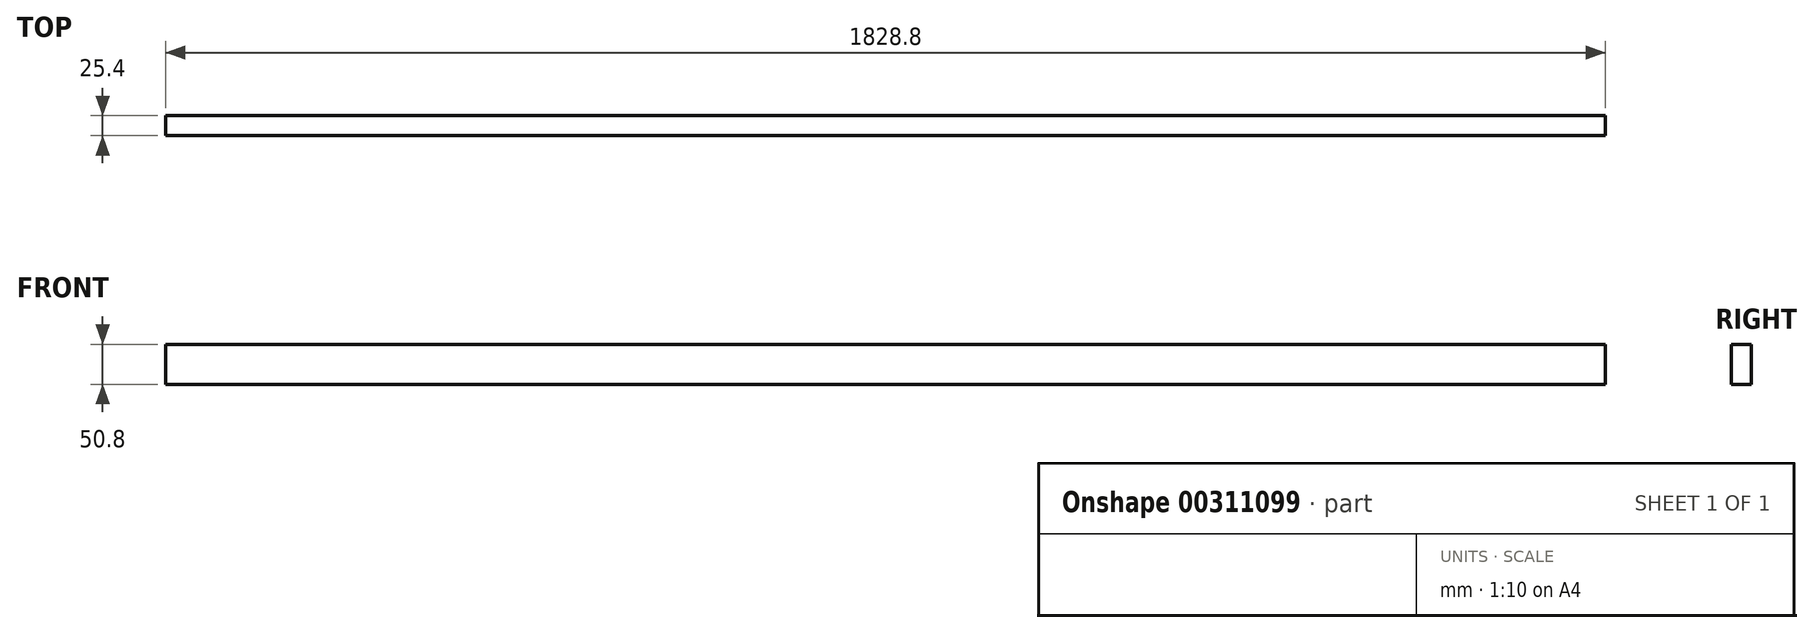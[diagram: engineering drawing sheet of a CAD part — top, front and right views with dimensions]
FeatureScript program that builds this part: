
annotation { "Feature Type Name" : "Feature", "Feature Type Description" : "" }
export const myFeature = defineFeature(function(context is Context, id is Id, definition is map)
    precondition{}
    {
        {
            var Q0;
            Q0=qCreatedBy(makeId("Front.planeOp"),FACE);
            var sketch = newSketch(context, id + "F0", { "sketchPlane" : qUnion([Q0])});
            skLineSegment(sketch, "E0.bottom", {"start": v(0, 0) * mm, "end": v(1828.8, 0) * mm});
            skLineSegment(sketch, "E0.top", {"start": v(0, -50.8) * mm, "end": v(1828.8, -50.8) * mm});
            skLineSegment(sketch, "E0.left", {"start": v(0, 0) * mm, "end": v(0, -50.8) * mm});
            skLineSegment(sketch, "E0.right", {"start": v(1828.8, 0) * mm, "end": v(1828.8, -50.8) * mm});
            skSolve(sketch);
        }
        {
            var Q0;
            Q0=makeQuery(id+"F0.imprint","IMPRINT",FACE,{"disambiguationData":[TD([[makeQuery(id+"F0.imprint","IMPRINT",EDGE,{"derivedFrom":sQuery(id+"F0.wireOp",EDGE,"E0.bottom")}),-1.0]])]});
            extrude(context, id + "F1", {"entities" : qUnion([Q0]), "depth" : 25.4 * mm});
        }
    });
